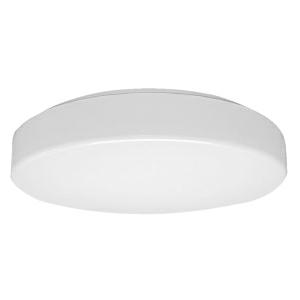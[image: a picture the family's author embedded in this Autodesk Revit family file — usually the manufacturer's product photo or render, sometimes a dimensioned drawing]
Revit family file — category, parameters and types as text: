
# Revit family: oblo_fit_-_oba_1000_830_d_00813346_b2e0
name_source: partatom
category: Lighting Fixtures
units: mm (PartAtom-declared; Revit-internal decimal feet)

## family parameters
Cut with Voids When Loaded = No
Host = Face
Light Source = No
Part Type = Normal
Room Calculation Point = No
Round Connector Dimension = Use Diameter
Shared = No

## types (1)
- OBLO.fit - OBA 1000/830/D (1 x LED, 1500 lm, 3000K)
    Apparent Load = 11 VA
    Approval mark = CE
    CIE Flux Codes = 41 72 91 84 100
    Color Rendering = 80-89
    Color Temperature = 3000K
    Control Gear = Electronic ballast
    Default Elevation = 1800 mm
    Description = OBA 1000/830/D|Surface-mounted luminaire.|light source:   Warm white   |work equipment: Power supply unit|luminous flux: 1500 lm|light distribution: Direct|class of protection: I|technology: Continuously dimmable|mains lead: Direct power supply|glare control: without|special features: DALI Load 1x, Integration into DALI light management systems|
    Frequency = 50 Hz, 60 Hz
    Height = 85 mm
    Lamp = 1 x LED
    Lamp Light Flux = 1500 lm
    Lamp count = 1
    Length = 300 mm
    Luminous efficacy = 136 lm/W
    Manufacturer = Waldmann
    ModVariant = No
    Model = 00813346
    Mounting Place = Ceiling
    Mounting Type = Surface mounted
    Number of Poles = 1
    OnlyDefault = Yes
    Power Factor = 1
    Product Name = OBLO.fit - OBA 1000/830/D
    Product group = Ceiling mounted luminaire
    ProductGroupID = 3
    Protection Class = Protection class I
    Protection Degree = IP 40
    RLX_Detail_Level = 1
    RLX_Emergency_Light_Flux = 0 lm
    RLX_Emergency_Type = 0
    RLX_Emergency_Type_DB = No
    RlxData = <blob elided: 22405 chars, md5=65244a74>
    Socket = socket
    Standby Power = 0 W
    System Light Flux = 1500 lm
    System Power = 11 W
    Type Comments = Product without accessories
    Type Image = oblo_led.jpg
    URL = http://relux.com
    VarID = ---
    Voltage = 230 V
    Voltage Range = 220-240 V
    Weight = 0.00 kg
    Width = 0 mm  [stored 0 ft]

note: [stored X ft] marks values corroborated as IEEE doubles in the binary element streams (Revit-internal decimal feet)

## geometry (parser evidence)
native form markers: Blend x4, Sweep x15
no freeform markers — native parametric forms only
